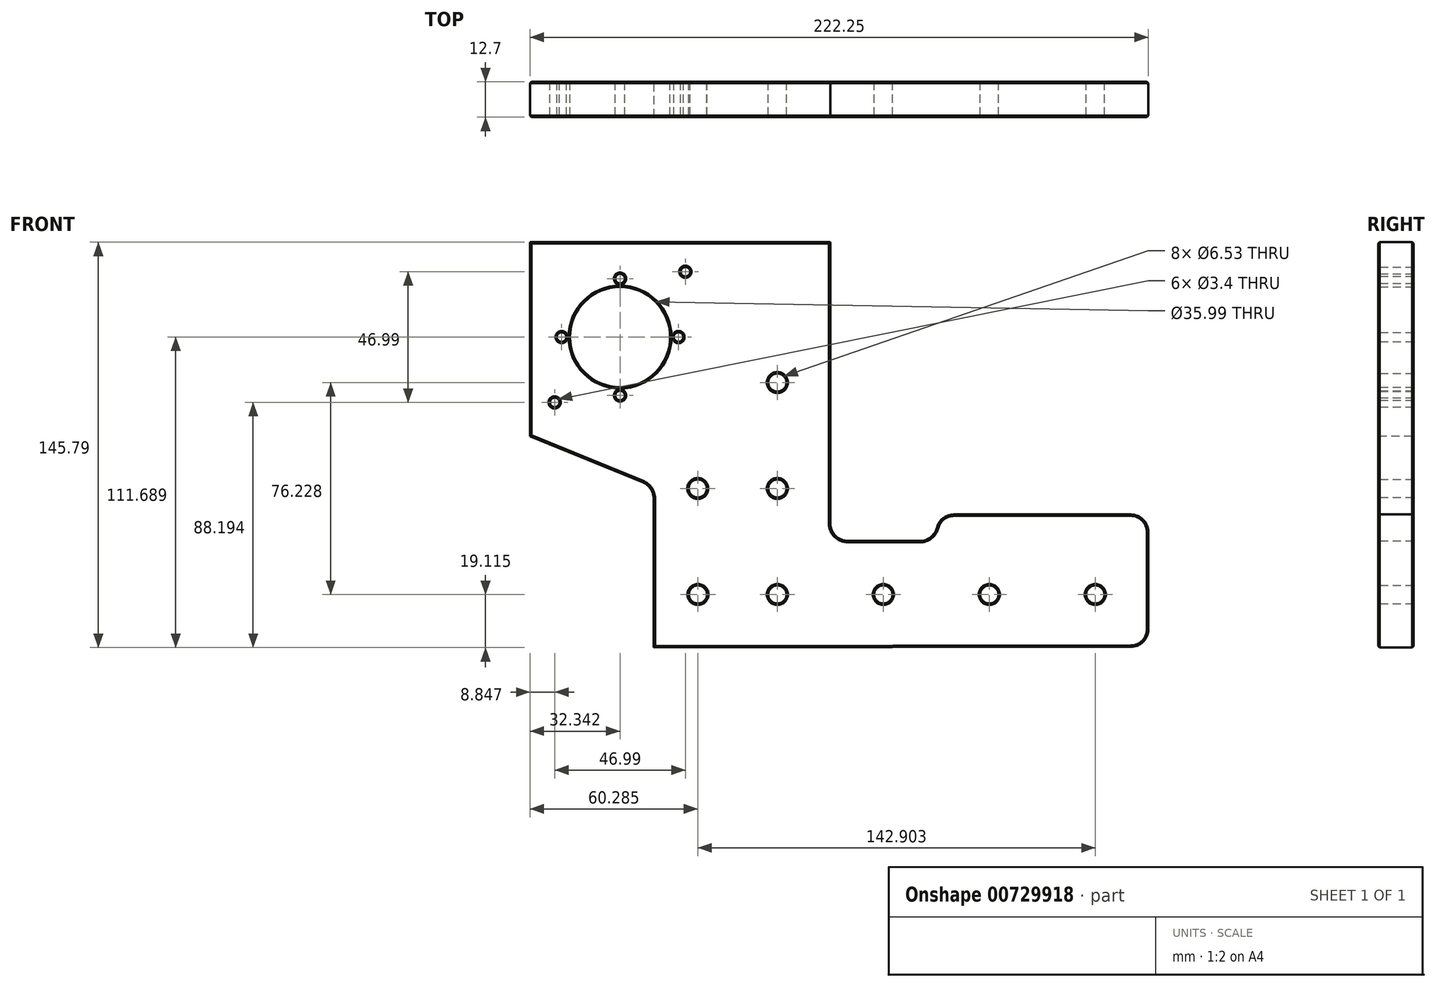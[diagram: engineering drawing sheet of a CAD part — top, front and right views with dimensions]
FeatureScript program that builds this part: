
annotation { "Feature Type Name" : "Feature", "Feature Type Description" : "" }
export const myFeature = defineFeature(function(context is Context, id is Id, definition is map)
    precondition{}
    {
        {
            var Q0;
            Q0=qCreatedBy(makeId("Front.planeOp"),FACE);
            var sketch = newSketch(context, id + "F0", { "sketchPlane" : qUnion([Q0])});
            skLineSegment(sketch, "E0.bottom", {"start": v(95.58, -98.45) * mm, "end": v(-126.67, -98.77) * mm});
            skLineSegment(sketch, "E1", {"start": v(-18.72, 66.33) * mm, "end": v(-18.72, -60.35) * mm});
            skLineSegment(sketch, "E2", {"start": v(95.58, -60.35) * mm, "end": v(95.58, -98.45) * mm});
            skLineSegment(sketch, "E3", {"start": v(-126.67, -98.77) * mm, "end": v(-126.67, 66.33) * mm});
            skLineSegment(sketch, "E4", {"start": v(-126.67, 66.33) * mm, "end": v(-18.72, 66.33) * mm});
            skCircle(sketch, "E5", {"center": v(-37.78, -3.37) * mm, "radius": 3.26 * mm});
            skCircle(sketch, "E6", {"center": v(-37.78, -41.47) * mm, "radius": 3.26 * mm});
            skCircle(sketch, "E7", {"center": v(-37.78, -79.6) * mm, "radius": 3.26 * mm});
            skCircle(sketch, "E8", {"center": v(0.32, -79.6) * mm, "radius": 3.26 * mm});
            skCircle(sketch, "E9", {"center": v(38.42, -79.6) * mm, "radius": 3.26 * mm});
            skCircle(sketch, "E10", {"center": v(76.52, -79.6) * mm, "radius": 3.26 * mm});
            skLineSegment(sketch, "E11", {"start": v(-18.72, -60.35) * mm, "end": v(19.38, -60.35) * mm});
            skLineSegment(sketch, "E12", {"start": v(95.58, -60.35) * mm, "end": v(95.58, -60.35) * mm});
            skLineSegment(sketch, "E13", {"start": v(19.38, -60.35) * mm, "end": v(19.38, -50.83) * mm});
            skLineSegment(sketch, "E14", {"start": v(19.38, -50.83) * mm, "end": v(95.58, -50.83) * mm});
            skLineSegment(sketch, "E15", {"start": v(95.58, -50.83) * mm, "end": v(95.58, -60.35) * mm});
            skCircle(sketch, "E16", {"center": v(-94.33, 12.98) * mm, "radius": 18 * mm});
            skLineSegment(sketch, "E17", {"start": v(-94.33, -17.86) * mm, "end": v(-94.33, 47.16) * mm, "construction": true});
            skLineSegment(sketch, "E18", {"start": v(-126.67, 12.98) * mm, "end": v(-62, 12.98) * mm, "construction": true});
            skLineSegment(sketch, "E19", {"start": v(-120.99, 39.64) * mm, "end": v(-63.9, -17.46) * mm, "construction": true});
            skLineSegment(sketch, "E20", {"start": v(-125.73, -18.42) * mm, "end": v(-61.49, 45.82) * mm, "construction": true});
            skCircle(sketch, "E21", {"center": v(-117.82, 36.47) * mm, "radius": 1.7 * mm});
            skCircle(sketch, "E22.MirrorC", {"center": v(-70.83, 36.47) * mm, "radius": 1.7 * mm});
            skCircle(sketch, "E23.MirrorC", {"center": v(-117.82, -10.52) * mm, "radius": 1.7 * mm});
            skCircle(sketch, "E24.MirrorC", {"center": v(-70.83, -10.52) * mm, "radius": 1.7 * mm});
            skCircle(sketch, "E25", {"center": v(-66.39, -41.47) * mm, "radius": 3.26 * mm});
            skCircle(sketch, "E26", {"center": v(-66.33, -79.6) * mm, "radius": 3.26 * mm});
            skCircle(sketch, "E27", {"center": v(-94.33, 33.98) * mm, "radius": 1.7 * mm});
            skCircle(sketch, "E28", {"center": v(-94.33, -8.03) * mm, "radius": 1.7 * mm});
            skCircle(sketch, "E29", {"center": v(-115.33, 12.98) * mm, "radius": 1.7 * mm});
            skCircle(sketch, "E30", {"center": v(-73.32, 12.98) * mm, "radius": 1.7 * mm});
            skSolve(sketch);
        }
        {
            var Q0;
            Q0=makeQuery(id+"F0.imprint","IMPRINT",FACE,{"disambiguationData":[TD([[makeQuery(id+"F0.imprint","IMPRINT",EDGE,{"derivedFrom":sQuery(id+"F0.wireOp",EDGE,"E0.bottom")}),-1.0]])]});
            var Q1;
            Q1=makeQuery(id+"F0.imprint","IMPRINT",FACE,{"disambiguationData":[TD([[makeQuery(id+"F0.imprint","IMPRINT",EDGE,{"derivedFrom":sQuery(id+"F0.wireOp",EDGE,"E21")}),1.0]])]});
            var Q2;
            Q2=makeQuery(id+"F0.imprint","IMPRINT",FACE,{"disambiguationData":[TD([[makeQuery(id+"F0.imprint","IMPRINT",EDGE,{"derivedFrom":sQuery(id+"F0.wireOp",EDGE,"E22.MirrorC")}),-1.0]])]});
            var Q3;
            Q3=makeQuery(id+"F0.imprint","IMPRINT",FACE,{"disambiguationData":[TD([[makeQuery(id+"F0.imprint","IMPRINT",EDGE,{"derivedFrom":sQuery(id+"F0.wireOp",EDGE,"E24.MirrorC")}),1.0]])]});
            var Q4;
            Q4=makeQuery(id+"F0.imprint","IMPRINT",FACE,{"disambiguationData":[TD([[makeQuery(id+"F0.imprint","IMPRINT",EDGE,{"derivedFrom":sQuery(id+"F0.wireOp",EDGE,"E23.MirrorC")}),-1.0]])]});
            extrude(context, id + "F1", {"entities" : qUnion([Q0, Q1, Q2, Q3, Q4]), "depth" : 12.7 * mm, "offsetDistance" : 25.4 * mm});
        }
        {
            var Q0;
            Q0=makeQuery(id+"F1.opExtrude","CAP_FACE",FACE,{"disambiguationData":[OSD([sQuery(id+"F0.wireOp",EDGE,"E0.bottom"),sQuery(id+"F0.wireOp",EDGE,"E1"),sQuery(id+"F0.wireOp",EDGE,"E2"),sQuery(id+"F0.wireOp",EDGE,"E3"),sQuery(id+"F0.wireOp",EDGE,"E4"),sQuery(id+"F0.wireOp",EDGE,"E5"),sQuery(id+"F0.wireOp",EDGE,"E6"),sQuery(id+"F0.wireOp",EDGE,"E7"),sQuery(id+"F0.wireOp",EDGE,"E8"),sQuery(id+"F0.wireOp",EDGE,"E9"),sQuery(id+"F0.wireOp",EDGE,"E10"),sQuery(id+"F0.wireOp",EDGE,"E11"),sQuery(id+"F0.wireOp",EDGE,"E13"),sQuery(id+"F0.wireOp",EDGE,"E14"),sQuery(id+"F0.wireOp",EDGE,"E15"),sQuery(id+"F0.wireOp",EDGE,"bdd12513-527b-488f-8d6b-20c45a8fa37b"),sQuery(id+"F0.wireOp",EDGE,"499d763e-db54-49f2-b91b-3f217bddd69d"),sQuery(id+"F0.wireOp",EDGE,"cc43b1b5-cebb-45d5-b199-afc85f6befad"),sQuery(id+"F0.wireOp",EDGE,"b27666f3-d0bd-404c-b8eb-62ebadabed05"),sQuery(id+"F0.wireOp",EDGE,"E16")])],"isStart":false});
            var sketch = newSketch(context, id + "F2", { "sketchPlane" : qUnion([Q0])});
            skLineSegment(sketch, "E31", {"start": v(-126.67, 47.08) * mm, "end": v(-18.72, 47.08) * mm});
            skLineSegment(sketch, "E32", {"start": v(-126.67, -22.66) * mm, "end": v(-82.26, -40.84) * mm});
            skLineSegment(sketch, "E33", {"start": v(-82.26, -40.84) * mm, "end": v(-82.26, -98.77) * mm});
            skSolve(sketch);
        }
        {
            var Q0;
            {var subQ0=sQuery(id+"F2.wireOp",EDGE,"E32");Q0=makeQuery(id+"F2.imprint","IMPRINT",FACE,{"disambiguationData":[TD([[makeQuery(id+"F2.imprint","IMPRINT",EDGE,{"derivedFrom":subQ0}),-1.0]])]});}
            var Q1;
            {var subQ0=sQuery(id+"F2.wireOp",EDGE,"E31");Q1=makeQuery(id+"F2.imprint","IMPRINT",FACE,{"disambiguationData":[TD([[makeQuery(id+"F2.imprint","IMPRINT",EDGE,{"derivedFrom":subQ0}),1.0]])]});}
            extrude(context, id + "F3", {"entities" : qUnion([Q0, Q1]), "operationType" : NewBodyOperationType.REMOVE, "oppositeDirection" : true, "depth" : 25.4 * mm, "offsetDistance" : 25.4 * mm});
        }
        {
            var Q0;
            Q0=makeQuery(id+"F3.boolean.opBoolean","COPY",EDGE,{"derivedFrom":makeQuery(id+"F3.opExtrude","SWEPT_EDGE",EDGE,{"disambiguationData":[OSD([sQuery(id+"F0.wireOp",EDGE,"E3"),sQuery(id+"F2.wireOp",EDGE,"E31")])]})});
            var Q1;
            Q1=makeQuery(id+"F3.boolean.opBoolean","COPY",EDGE,{"derivedFrom":makeQuery(id+"F3.opExtrude","SWEPT_EDGE",EDGE,{"disambiguationData":[OSD([sQuery(id+"F0.wireOp",EDGE,"E3"),sQuery(id+"F2.wireOp",EDGE,"E32")])]})});
            var Q2;
            Q2=makeQuery(id+"F3.boolean.opBoolean","COPY",EDGE,{"derivedFrom":makeQuery(id+"F3.opExtrude","SWEPT_EDGE",EDGE,{"disambiguationData":[OSD([sQuery(id+"F0.wireOp",EDGE,"E1"),sQuery(id+"F2.wireOp",EDGE,"E31")])]})});
            var Q3;
            Q3=makeQuery(id+"F3.boolean.opBoolean","COPY",EDGE,{"derivedFrom":makeQuery(id+"F3.opExtrude","SWEPT_EDGE",EDGE,{"disambiguationData":[OSD([sQuery(id+"F2.wireOp",EDGE,"E32"),sQuery(id+"F2.wireOp",EDGE,"E33")])]})});
            var Q4;
            Q4=makeQuery(id+"F3.boolean.opBoolean","COPY",EDGE,{"derivedFrom":makeQuery(id+"F3.opExtrude","SWEPT_EDGE",EDGE,{"disambiguationData":[OSD([sQuery(id+"F0.wireOp",EDGE,"E0.bottom"),sQuery(id+"F2.wireOp",EDGE,"E33")])]})});
            var Q5;
            Q5=makeQuery(id+"F1.opExtrude","SWEPT_EDGE",EDGE,{"disambiguationData":[OSD([sQuery(id+"F0.wireOp",EDGE,"E0.bottom"),sQuery(id+"F0.wireOp",EDGE,"E2")])]});
            var Q6;
            Q6=makeQuery(id+"F1.opExtrude","SWEPT_EDGE",EDGE,{"disambiguationData":[OSD([sQuery(id+"F0.wireOp",EDGE,"E14"),sQuery(id+"F0.wireOp",EDGE,"E15")])]});
            var Q7;
            Q7=makeQuery(id+"F1.opExtrude","SWEPT_EDGE",EDGE,{"disambiguationData":[OSD([sQuery(id+"F0.wireOp",EDGE,"E13"),sQuery(id+"F0.wireOp",EDGE,"E14")])]});
            var Q8;
            Q8=makeQuery(id+"F1.opExtrude","SWEPT_EDGE",EDGE,{"disambiguationData":[OSD([sQuery(id+"F0.wireOp",EDGE,"E1"),sQuery(id+"F0.wireOp",EDGE,"E11")])]});
            fillet(context, id + "F4", {"entities" : qUnion([Q0, Q1, Q2, Q3, Q4, Q5, Q6, Q7, Q8]), "radius" : 6.35 * mm, "tangentPropagation" : true, "allowEdgeOverflow" : false});
        }
        {
            var Q0;
            Q0=makeQuery(id+"F1.opExtrude","SWEPT_EDGE",EDGE,{"disambiguationData":[OSD([sQuery(id+"F0.wireOp",EDGE,"E11"),sQuery(id+"F0.wireOp",EDGE,"E13")])]});
            fillet(context, id + "F5", {"entities" : qUnion([Q0]), "radius" : 6.35 * mm, "tangentPropagation" : true, "allowEdgeOverflow" : false});
        }
        {
            var Q0;
            Q0=makeQuery(id+"F1.opExtrude","CAP_FACE",FACE,{"disambiguationData":[OSD([sQuery(id+"F0.wireOp",EDGE,"E0.bottom"),sQuery(id+"F0.wireOp",EDGE,"E1"),sQuery(id+"F0.wireOp",EDGE,"E2"),sQuery(id+"F0.wireOp",EDGE,"E3"),sQuery(id+"F0.wireOp",EDGE,"E4"),sQuery(id+"F0.wireOp",EDGE,"E5"),sQuery(id+"F0.wireOp",EDGE,"E6"),sQuery(id+"F0.wireOp",EDGE,"E7"),sQuery(id+"F0.wireOp",EDGE,"E8"),sQuery(id+"F0.wireOp",EDGE,"E9"),sQuery(id+"F0.wireOp",EDGE,"E10"),sQuery(id+"F0.wireOp",EDGE,"E11"),sQuery(id+"F0.wireOp",EDGE,"E13"),sQuery(id+"F0.wireOp",EDGE,"E14"),sQuery(id+"F0.wireOp",EDGE,"E15"),sQuery(id+"F0.wireOp",EDGE,"E16"),sQuery(id+"F0.wireOp",EDGE,"E21"),sQuery(id+"F0.wireOp",EDGE,"E22.MirrorC"),sQuery(id+"F0.wireOp",EDGE,"E23.MirrorC"),sQuery(id+"F0.wireOp",EDGE,"E24.MirrorC"),sQuery(id+"F0.wireOp",EDGE,"E25"),sQuery(id+"F0.wireOp",EDGE,"E26"),sQuery(id+"F0.wireOp",EDGE,"E27"),sQuery(id+"F0.wireOp",EDGE,"E28"),sQuery(id+"F0.wireOp",EDGE,"E29"),sQuery(id+"F0.wireOp",EDGE,"E30")])],"isStart":false});
            var Q1;
            Q1=makeQuery(id+"F1.opExtrude","CAP_FACE",FACE,{"disambiguationData":[OSD([sQuery(id+"F0.wireOp",EDGE,"E0.bottom"),sQuery(id+"F0.wireOp",EDGE,"E1"),sQuery(id+"F0.wireOp",EDGE,"E2"),sQuery(id+"F0.wireOp",EDGE,"E3"),sQuery(id+"F0.wireOp",EDGE,"E4"),sQuery(id+"F0.wireOp",EDGE,"E5"),sQuery(id+"F0.wireOp",EDGE,"E6"),sQuery(id+"F0.wireOp",EDGE,"E7"),sQuery(id+"F0.wireOp",EDGE,"E8"),sQuery(id+"F0.wireOp",EDGE,"E9"),sQuery(id+"F0.wireOp",EDGE,"E10"),sQuery(id+"F0.wireOp",EDGE,"E11"),sQuery(id+"F0.wireOp",EDGE,"E13"),sQuery(id+"F0.wireOp",EDGE,"E14"),sQuery(id+"F0.wireOp",EDGE,"E15"),sQuery(id+"F0.wireOp",EDGE,"E16"),sQuery(id+"F0.wireOp",EDGE,"E21"),sQuery(id+"F0.wireOp",EDGE,"E22.MirrorC"),sQuery(id+"F0.wireOp",EDGE,"E23.MirrorC"),sQuery(id+"F0.wireOp",EDGE,"E24.MirrorC"),sQuery(id+"F0.wireOp",EDGE,"E25"),sQuery(id+"F0.wireOp",EDGE,"E26"),sQuery(id+"F0.wireOp",EDGE,"E27"),sQuery(id+"F0.wireOp",EDGE,"E28"),sQuery(id+"F0.wireOp",EDGE,"E29"),sQuery(id+"F0.wireOp",EDGE,"E30")])],"isStart":true});
            var Q2;
            {var subQ0=sQuery(id+"F0.wireOp",EDGE,"E24.MirrorC");var subQ1=sQuery(id+"F0.wireOp",EDGE,"E23.MirrorC");var subQ2=sQuery(id+"F0.wireOp",EDGE,"E22.MirrorC");var subQ3=sQuery(id+"F0.wireOp",EDGE,"E21");Q2=makeQuery(id+"FnEefVxFa0R0ueH_1.boolean.opBoolean","MERGE",FACE,{"derivedFrom":[makeQuery(id+"FFe5l9Ppjfo7W1Y_1.opPattern","COPY",FACE,{"derivedFrom":makeQuery(id+"F1.opExtrude","CAP_FACE",FACE,{"disambiguationData":[OSD([sQuery(id+"F0.wireOp",EDGE,"E0.bottom"),sQuery(id+"F0.wireOp",EDGE,"E1"),sQuery(id+"F0.wireOp",EDGE,"E2"),sQuery(id+"F0.wireOp",EDGE,"E3"),sQuery(id+"F0.wireOp",EDGE,"E4"),sQuery(id+"F0.wireOp",EDGE,"E5"),sQuery(id+"F0.wireOp",EDGE,"E6"),sQuery(id+"F0.wireOp",EDGE,"E7"),sQuery(id+"F0.wireOp",EDGE,"E8"),sQuery(id+"F0.wireOp",EDGE,"E9"),sQuery(id+"F0.wireOp",EDGE,"E10"),sQuery(id+"F0.wireOp",EDGE,"E11"),sQuery(id+"F0.wireOp",EDGE,"E13"),sQuery(id+"F0.wireOp",EDGE,"E14"),sQuery(id+"F0.wireOp",EDGE,"E15"),sQuery(id+"F0.wireOp",EDGE,"E16"),subQ3,subQ2,subQ1,subQ0,sQuery(id+"F0.wireOp",EDGE,"E25"),sQuery(id+"F0.wireOp",EDGE,"E26"),sQuery(id+"F0.wireOp",EDGE,"E27"),sQuery(id+"F0.wireOp",EDGE,"E28"),sQuery(id+"F0.wireOp",EDGE,"E29"),sQuery(id+"F0.wireOp",EDGE,"E30")])],"isStart":false}),"instanceName":"1"}),makeQuery(id+"FnEefVxFa0R0ueH_1.opExtrude","CAP_FACE",FACE,{"disambiguationData":[OSD([subQ3])],"isStart":true}),makeQuery(id+"FnEefVxFa0R0ueH_1.opExtrude","CAP_FACE",FACE,{"disambiguationData":[OSD([subQ2])],"isStart":true}),makeQuery(id+"FnEefVxFa0R0ueH_1.opExtrude","CAP_FACE",FACE,{"disambiguationData":[OSD([subQ1])],"isStart":true}),makeQuery(id+"FnEefVxFa0R0ueH_1.opExtrude","CAP_FACE",FACE,{"disambiguationData":[OSD([subQ0])],"isStart":true})]});}
            var Q3;
            {var subQ0=sQuery(id+"F0.wireOp",EDGE,"E24.MirrorC");var subQ1=sQuery(id+"F0.wireOp",EDGE,"E23.MirrorC");var subQ2=sQuery(id+"F0.wireOp",EDGE,"E22.MirrorC");var subQ3=sQuery(id+"F0.wireOp",EDGE,"E21");Q3=makeQuery(id+"FnEefVxFa0R0ueH_1.boolean.opBoolean","MERGE",FACE,{"derivedFrom":[makeQuery(id+"FFe5l9Ppjfo7W1Y_1.opPattern","COPY",FACE,{"derivedFrom":makeQuery(id+"F1.opExtrude","CAP_FACE",FACE,{"disambiguationData":[OSD([sQuery(id+"F0.wireOp",EDGE,"E0.bottom"),sQuery(id+"F0.wireOp",EDGE,"E1"),sQuery(id+"F0.wireOp",EDGE,"E2"),sQuery(id+"F0.wireOp",EDGE,"E3"),sQuery(id+"F0.wireOp",EDGE,"E4"),sQuery(id+"F0.wireOp",EDGE,"E5"),sQuery(id+"F0.wireOp",EDGE,"E6"),sQuery(id+"F0.wireOp",EDGE,"E7"),sQuery(id+"F0.wireOp",EDGE,"E8"),sQuery(id+"F0.wireOp",EDGE,"E9"),sQuery(id+"F0.wireOp",EDGE,"E10"),sQuery(id+"F0.wireOp",EDGE,"E11"),sQuery(id+"F0.wireOp",EDGE,"E13"),sQuery(id+"F0.wireOp",EDGE,"E14"),sQuery(id+"F0.wireOp",EDGE,"E15"),sQuery(id+"F0.wireOp",EDGE,"E16"),subQ3,subQ2,subQ1,subQ0,sQuery(id+"F0.wireOp",EDGE,"E25"),sQuery(id+"F0.wireOp",EDGE,"E26"),sQuery(id+"F0.wireOp",EDGE,"E27"),sQuery(id+"F0.wireOp",EDGE,"E28"),sQuery(id+"F0.wireOp",EDGE,"E29"),sQuery(id+"F0.wireOp",EDGE,"E30")])],"isStart":true}),"instanceName":"1"}),makeQuery(id+"FnEefVxFa0R0ueH_1.opExtrude","CAP_FACE",FACE,{"disambiguationData":[OSD([subQ3])],"isStart":false}),makeQuery(id+"FnEefVxFa0R0ueH_1.opExtrude","CAP_FACE",FACE,{"disambiguationData":[OSD([subQ2])],"isStart":false}),makeQuery(id+"FnEefVxFa0R0ueH_1.opExtrude","CAP_FACE",FACE,{"disambiguationData":[OSD([subQ1])],"isStart":false}),makeQuery(id+"FnEefVxFa0R0ueH_1.opExtrude","CAP_FACE",FACE,{"disambiguationData":[OSD([subQ0])],"isStart":false})]});}
            chamfer(context, id + "F6", {"entities" : qUnion([Q0, Q1, Q2, Q3]), "width" : 0.5 * mm, "tangentPropagation" : true});
        }
    });
